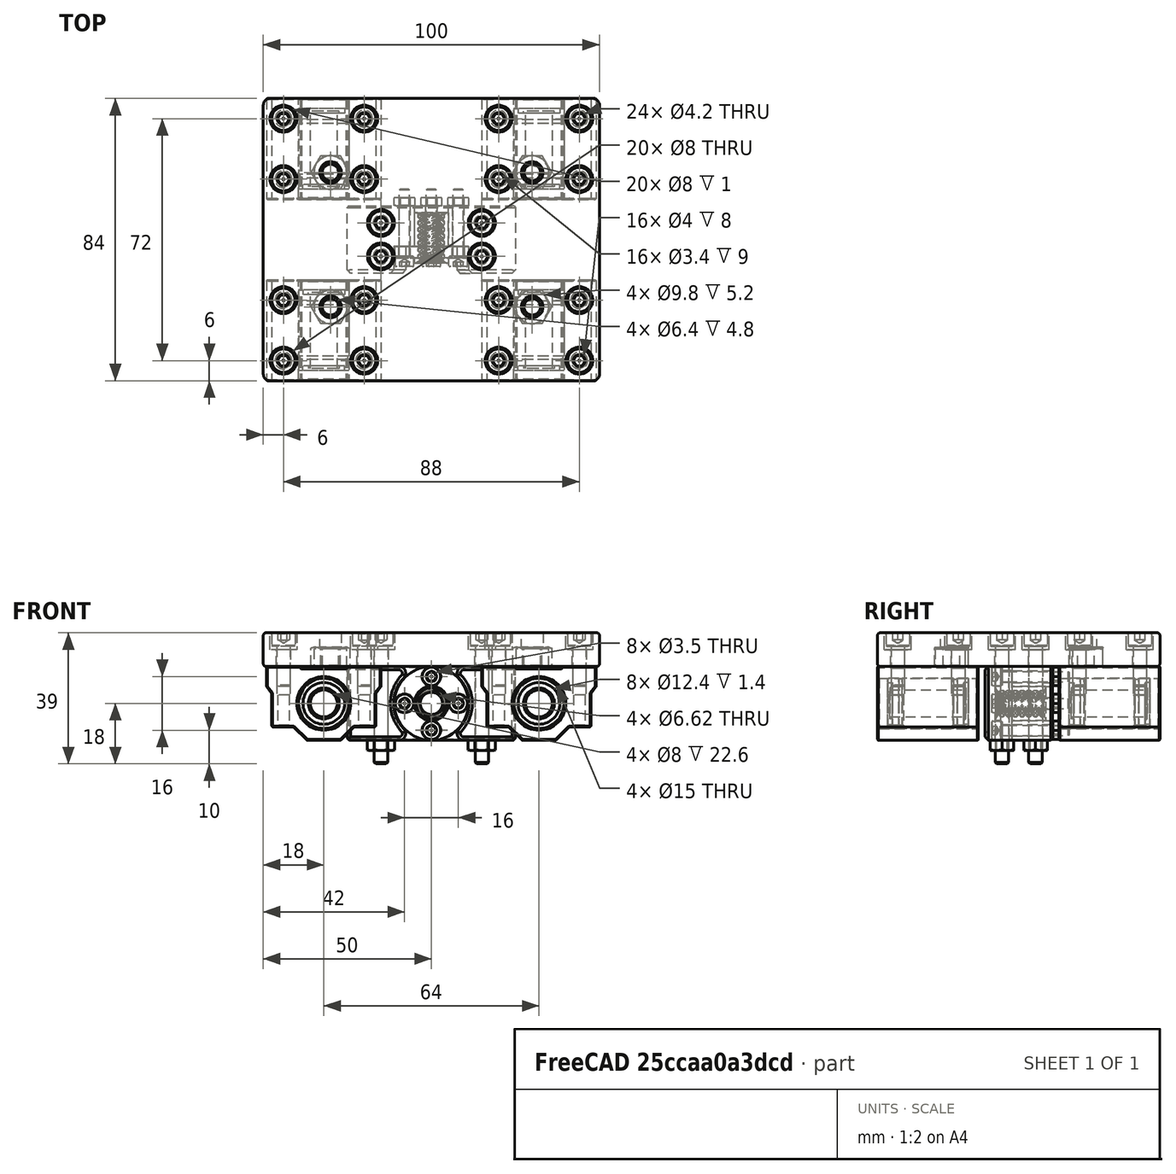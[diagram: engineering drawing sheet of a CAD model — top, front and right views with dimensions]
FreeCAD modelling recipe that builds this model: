
FCSTD DOCUMENT  (FreeCAD 0.19R)
Label: carriage_ass4
License: All rights reserved
LicenseURL: http://en.wikipedia.org/wiki/All_rights_reserved
objects: Part::FeaturePython×36, Part::Compound×18, Part::Feature×11
note: 65 computed .brp shape members not serialized (recipe doc carries the construction recipe); baked Part::Feature solids carry a one-line shape summary decoded from their .brp

FEATURE [Part::Feature] Chamfer002001  label="nutblock"
  Placement = pos=(25,32,-22) rot=(0,0,1;0rad)
  shape: bbox 50 x 20 x 22 mm, 53 faces (baked)
FEATURE [Part::Feature] Cut001  label="trapeznut"
  Placement = pos=(50,35,-11) rot=(0,0,1;1.5708rad)
  shape: bbox 22 x 24 x 22 mm, 53 faces (baked)
FEATURE [Part::FeaturePython] Screw  label="M4x12-Screw"  # Fasteners workbench fastener (typed FeaturePython)
  Placement = pos=(6,6,6) rot=(0,0,1;0rad)
  Visibility1 = false
  diameter = 5
  invert = false
  length = 3
  matchOuter = false
  offset = 0
  thread = false
  type = 15
FEATURE [Part::FeaturePython] Screw001  label="M4x12-Screw001"  # Fasteners workbench fastener (typed FeaturePython)
  Placement = pos=(30,6,6) rot=(0,0,1;0rad)
  Visibility1 = false
  diameter = 5
  invert = false
  length = 3
  matchOuter = false
  offset = 0
  thread = false
  type = 15
FEATURE [Part::FeaturePython] Screw002  label="M4x12-Screw002"  # Fasteners workbench fastener (typed FeaturePython)
  Placement = pos=(30,24,6) rot=(0,0,1;0rad)
  Visibility1 = false
  diameter = 5
  invert = false
  length = 3
  matchOuter = false
  offset = 0
  thread = false
  type = 15
FEATURE [Part::FeaturePython] Screw003  label="M4x12-Screw003"  # Fasteners workbench fastener (typed FeaturePython)
  Placement = pos=(6,24,6) rot=(0,0,1;0rad)
  Visibility1 = false
  diameter = 5
  invert = false
  length = 3
  matchOuter = false
  offset = 0
  thread = false
  type = 15
FEATURE [Part::Compound] Compound  label="m4x12_4er"
  Links = -> [Screw,Screw001,Screw002,Screw003]
FEATURE [Part::FeaturePython] Screw004  label="M4x12-Screw004"  # Fasteners workbench fastener (typed FeaturePython)
  Placement = pos=(30,6,6) rot=(0,0,1;0rad)
  Visibility1 = false
  diameter = 5
  invert = false
  length = 3
  matchOuter = false
  offset = 0
  thread = false
  type = 15
FEATURE [Part::FeaturePython] Screw005  label="M4x12-Screw005"  # Fasteners workbench fastener (typed FeaturePython)
  Placement = pos=(6,6,6) rot=(0,0,1;0rad)
  Visibility1 = false
  diameter = 5
  invert = false
  length = 3
  matchOuter = false
  offset = 0
  thread = false
  type = 15
FEATURE [Part::FeaturePython] Screw006  label="M4x12-Screw006"  # Fasteners workbench fastener (typed FeaturePython)
  Placement = pos=(30,24,6) rot=(0,0,1;0rad)
  Visibility1 = false
  diameter = 5
  invert = false
  length = 3
  matchOuter = false
  offset = 0
  thread = false
  type = 15
FEATURE [Part::FeaturePython] Screw007  label="M4x12-Screw007"  # Fasteners workbench fastener (typed FeaturePython)
  Placement = pos=(6,24,6) rot=(0,0,1;0rad)
  Visibility1 = false
  diameter = 5
  invert = false
  length = 3
  matchOuter = false
  offset = 0
  thread = false
  type = 15
FEATURE [Part::Compound] Compound001  label="m4x12_4er001"
  Links = -> [Screw005,Screw004,Screw006,Screw007]
  Placement = pos=(64,0,0) rot=(0,0,1;0rad)
FEATURE [Part::FeaturePython] Screw008  label="M4x12-Screw008"  # Fasteners workbench fastener (typed FeaturePython)
  Placement = pos=(30,6,6) rot=(0,0,1;0rad)
  Visibility1 = false
  diameter = 5
  invert = false
  length = 3
  matchOuter = false
  offset = 0
  thread = false
  type = 15
FEATURE [Part::FeaturePython] Screw009  label="M4x12-Screw009"  # Fasteners workbench fastener (typed FeaturePython)
  Placement = pos=(30,24,6) rot=(0,0,1;0rad)
  Visibility1 = false
  diameter = 5
  invert = false
  length = 3
  matchOuter = false
  offset = 0
  thread = false
  type = 15
FEATURE [Part::FeaturePython] Screw010  label="M4x12-Screw010"  # Fasteners workbench fastener (typed FeaturePython)
  Placement = pos=(6,24,6) rot=(0,0,1;0rad)
  Visibility1 = false
  diameter = 5
  invert = false
  length = 3
  matchOuter = false
  offset = 0
  thread = false
  type = 15
FEATURE [Part::FeaturePython] Screw011  label="M4x12-Screw011"  # Fasteners workbench fastener (typed FeaturePython)
  Placement = pos=(6,6,6) rot=(0,0,1;0rad)
  Visibility1 = false
  diameter = 5
  invert = false
  length = 3
  matchOuter = false
  offset = 0
  thread = false
  type = 15
FEATURE [Part::Compound] Compound002  label="m4x12_4er002"
  Links = -> [Screw011,Screw008,Screw009,Screw010]
  Placement = pos=(64,54,0) rot=(0,0,1;0rad)
FEATURE [Part::FeaturePython] Screw012  label="M4x12-Screw012"  # Fasteners workbench fastener (typed FeaturePython)
  Placement = pos=(6,6,6) rot=(0,0,1;0rad)
  Visibility1 = false
  diameter = 5
  invert = false
  length = 3
  matchOuter = false
  offset = 0
  thread = false
  type = 15
FEATURE [Part::FeaturePython] Screw013  label="M4x12-Screw013"  # Fasteners workbench fastener (typed FeaturePython)
  Placement = pos=(30,6,6) rot=(0,0,1;0rad)
  Visibility1 = false
  diameter = 5
  invert = false
  length = 3
  matchOuter = false
  offset = 0
  thread = false
  type = 15
FEATURE [Part::FeaturePython] Screw014  label="M4x12-Screw014"  # Fasteners workbench fastener (typed FeaturePython)
  Placement = pos=(30,24,6) rot=(0,0,1;0rad)
  Visibility1 = false
  diameter = 5
  invert = false
  length = 3
  matchOuter = false
  offset = 0
  thread = false
  type = 15
FEATURE [Part::FeaturePython] Screw015  label="M4x12-Screw015"  # Fasteners workbench fastener (typed FeaturePython)
  Placement = pos=(6,24,6) rot=(0,0,1;0rad)
  Visibility1 = false
  diameter = 5
  invert = false
  length = 3
  matchOuter = false
  offset = 0
  thread = false
  type = 15
FEATURE [Part::Compound] Compound003  label="m4x12_4er003"
  Links = -> [Screw012,Screw013,Screw014,Screw015]
  Placement = pos=(0,54,0) rot=(0,0,1;0rad)
FEATURE [Part::Compound] Compound004  label="m4x12ers"
  Links = -> [Compound,Compound001,Compound002,Compound003]
FEATURE [Part::FeaturePython] Screw016  label="M4x35-Screw"  # Fasteners workbench fastener (typed FeaturePython)
  Placement = pos=(35,37,6) rot=(0,0,1;0rad)
  Visibility1 = false
  diameter = 5
  invert = false
  length = 9
  matchOuter = false
  offset = 0
  thread = false
  type = 15
FEATURE [Part::FeaturePython] Screw017  label="M4x35-Screw001"  # Fasteners workbench fastener (typed FeaturePython)
  Placement = pos=(65,37,6) rot=(0,0,1;0rad)
  Visibility1 = false
  diameter = 5
  invert = false
  length = 9
  matchOuter = false
  offset = 0
  thread = false
  type = 15
FEATURE [Part::FeaturePython] Screw018  label="M4x35-Screw002"  # Fasteners workbench fastener (typed FeaturePython)
  Placement = pos=(65,47,6) rot=(0,0,1;0rad)
  Visibility1 = false
  diameter = 5
  invert = false
  length = 9
  matchOuter = false
  offset = 0
  thread = false
  type = 15
FEATURE [Part::FeaturePython] Screw019  label="M4x35-Screw003"  # Fasteners workbench fastener (typed FeaturePython)
  Placement = pos=(35,47,6) rot=(0,0,1;0rad)
  Visibility1 = false
  diameter = 5
  invert = false
  length = 9
  matchOuter = false
  offset = 0
  thread = false
  type = 15
FEATURE [Part::Compound] Compound005  label="m4x35ers"
  Links = -> [Screw016,Screw017,Screw018,Screw019]
FEATURE [Part::FeaturePython] Nut001  label="M4-Nut"  # Fasteners workbench fastener (typed FeaturePython)
  Placement = pos=(35,37,-25) rot=(0,0,1;0rad)
  Visibility1 = false
  diameter = 6
  invert = false
  matchOuter = false
  offset = 0
  thread = false
  type = 4
FEATURE [Part::FeaturePython] Nut002  label="M4-Nut001"  # Fasteners workbench fastener (typed FeaturePython)
  Placement = pos=(35,47,-25) rot=(0,0,1;0rad)
  Visibility1 = false
  diameter = 6
  invert = false
  matchOuter = false
  offset = 0
  thread = false
  type = 4
FEATURE [Part::FeaturePython] Nut003  label="M4-Nut002"  # Fasteners workbench fastener (typed FeaturePython)
  Placement = pos=(65,47,-25) rot=(0,0,1;0rad)
  Visibility1 = false
  diameter = 6
  invert = false
  matchOuter = false
  offset = 0
  thread = false
  type = 4
FEATURE [Part::FeaturePython] Nut004  label="M4-Nut003"  # Fasteners workbench fastener (typed FeaturePython)
  Placement = pos=(65,37,-25) rot=(0,0,1;0rad)
  Visibility1 = false
  diameter = 6
  invert = false
  matchOuter = false
  offset = 0
  thread = false
  type = 4
FEATURE [Part::Compound] Compound006  label="m4nuts"
  Links = -> [Nut001,Nut002,Nut003,Nut004]
FEATURE [Part::FeaturePython] Nut  label="M6-Nut"  # Fasteners workbench fastener (typed FeaturePython)
  Placement = pos=(20,22,0) rot=(0,0,1;0rad)
  Visibility1 = false
  diameter = 2
  invert = false
  matchOuter = false
  offset = 0
  thread = false
  type = 2
FEATURE [Part::FeaturePython] Nut005  label="M6-Nut001"  # Fasteners workbench fastener (typed FeaturePython)
  Placement = pos=(80,22,0) rot=(0,0,1;0rad)
  Visibility1 = false
  diameter = 2
  invert = false
  matchOuter = false
  offset = 0
  thread = false
  type = 2
FEATURE [Part::FeaturePython] Nut006  label="M6-Nut004"  # Fasteners workbench fastener (typed FeaturePython)
  Placement = pos=(20,62,0) rot=(0,0,1;0rad)
  Visibility1 = false
  diameter = 2
  invert = false
  matchOuter = false
  offset = 0
  thread = false
  type = 2
FEATURE [Part::FeaturePython] Nut007  label="M6-Nut003"  # Fasteners workbench fastener (typed FeaturePython)
  Placement = pos=(80,62,0) rot=(0,0,1;0rad)
  Visibility1 = false
  diameter = 2
  invert = false
  matchOuter = false
  offset = 0
  thread = false
  type = 2
FEATURE [Part::Compound] Compound007  label="m6nuts"
  Links = -> [Nut,Nut005,Nut006,Nut007]
FEATURE [Part::FeaturePython] Screw020  label="M3x20-Screw"  # Fasteners workbench fastener (typed FeaturePython)
  Placement = pos=(50,37,-19) rot=(1,0,0;1.5708rad)
  Visibility1 = false
  diameter = 4
  invert = false
  length = 7
  matchOuter = false
  offset = 0
  thread = false
  type = 15
FEATURE [Part::FeaturePython] Nut008  label="M3-Nut"  # Fasteners workbench fastener (typed FeaturePython)
  Placement = pos=(50,54.5,-19) rot=(1,0,0;1.5708rad)
  Visibility1 = false
  diameter = 4
  invert = false
  matchOuter = false
  offset = 0
  thread = false
  type = 4
FEATURE [Part::Compound] Compound008  label="m3x20screwnut"
  Links = -> [Screw020,Nut008]
  Placement = pos=(8,0,8) rot=(0,0,1;0rad)
FEATURE [Part::FeaturePython] Screw021  label="M3x20-Screw001"  # Fasteners workbench fastener (typed FeaturePython)
  Placement = pos=(50,37,-19) rot=(1,0,0;1.5708rad)
  Visibility1 = false
  diameter = 4
  invert = false
  length = 7
  matchOuter = false
  offset = 0
  thread = false
  type = 15
FEATURE [Part::FeaturePython] Nut009  label="M3-Nut001"  # Fasteners workbench fastener (typed FeaturePython)
  Placement = pos=(50,54.5,-19) rot=(1,0,0;1.5708rad)
  Visibility1 = false
  diameter = 4
  invert = false
  matchOuter = false
  offset = 0
  thread = false
  type = 4
FEATURE [Part::Compound] Compound009  label="m3x20screwnut001"
  Links = -> [Screw021,Nut009]
  Placement = pos=(0,0,16) rot=(0,0,1;0rad)
FEATURE [Part::FeaturePython] Screw022  label="M3x20-Screw002"  # Fasteners workbench fastener (typed FeaturePython)
  Placement = pos=(50,37,-19) rot=(1,0,0;1.5708rad)
  Visibility1 = false
  diameter = 4
  invert = false
  length = 7
  matchOuter = false
  offset = 0
  thread = false
  type = 15
FEATURE [Part::FeaturePython] Nut010  label="M3-Nut002"  # Fasteners workbench fastener (typed FeaturePython)
  Placement = pos=(50,54.5,-19) rot=(1,0,0;1.5708rad)
  Visibility1 = false
  diameter = 4
  invert = false
  matchOuter = false
  offset = 0
  thread = false
  type = 4
FEATURE [Part::Compound] Compound010  label="m3x20screwnut002"
  Links = -> [Screw022,Nut010]
FEATURE [Part::FeaturePython] Screw023  label="M3x20-Screw003"  # Fasteners workbench fastener (typed FeaturePython)
  Placement = pos=(50,37,-19) rot=(1,0,0;1.5708rad)
  Visibility1 = false
  diameter = 4
  invert = false
  length = 7
  matchOuter = false
  offset = 0
  thread = false
  type = 15
FEATURE [Part::FeaturePython] Nut011  label="M3-Nut003"  # Fasteners workbench fastener (typed FeaturePython)
  Placement = pos=(50,54.5,-19) rot=(1,0,0;1.5708rad)
  Visibility1 = false
  diameter = 4
  invert = false
  matchOuter = false
  offset = 0
  thread = false
  type = 4
FEATURE [Part::Compound] Compound011  label="m3x20screwnut003"
  Links = -> [Screw023,Nut011]
  Placement = pos=(-8,0,8) rot=(0,0,1;0rad)
FEATURE [Part::Compound] Compound012  label="m3x20screwnuts"
  Links = -> [Compound008,Compound009,Compound010,Compound011]
FEATURE [Part::Feature] Fillet002001  label="carriageplate2"
  shape: bbox 100.3 x 84.33 x 10 mm, 118 faces (baked)
FEATURE [Part::Feature] Body001  label="SC8UU"
  shape: bbox 34 x 30 x 22 mm, 85 faces (baked)
FEATURE [Part::Feature] Revolution001  label="LM8UU"
  Placement = pos=(0,-15,-10.5) rot=(1,0,0;3.14159rad)
  shape: bbox 15 x 24 x 15 mm, 20 faces (baked)
FEATURE [Part::Compound] Compound013  label="SC8UU+LM8UU"
  Links = -> [Revolution001,Body001]
  Placement = pos=(18,30,-0.5) rot=(0,0,1;0rad)
FEATURE [Part::Feature] Body002  label="SC8UU001"
  shape: bbox 34 x 30 x 22 mm, 85 faces (baked)
FEATURE [Part::Feature] Revolution002  label="LM8UU001"
  Placement = pos=(0,-15,-10.5) rot=(1,0,0;3.14159rad)
  shape: bbox 15 x 24 x 15 mm, 20 faces (baked)
FEATURE [Part::Compound] Compound014  label="SC8UU+LM8UU001"
  Links = -> [Revolution002,Body002]
  Placement = pos=(82,30,-0.5) rot=(0,0,1;0rad)
FEATURE [Part::Feature] Revolution003  label="LM8UU002"
  Placement = pos=(0,-15,-10.5) rot=(1,0,0;3.14159rad)
  shape: bbox 15 x 24 x 15 mm, 20 faces (baked)
FEATURE [Part::Feature] Body003  label="SC8UU002"
  shape: bbox 34 x 30 x 22 mm, 85 faces (baked)
FEATURE [Part::Compound] Compound015  label="SC8UU+LM8UU002"
  Links = -> [Revolution003,Body003]
  Placement = pos=(82,84,-0.5) rot=(0,0,1;0rad)
FEATURE [Part::Feature] Body004  label="SC8UU003"
  shape: bbox 34 x 30 x 22 mm, 85 faces (baked)
FEATURE [Part::Feature] Revolution004  label="LM8UU003"
  Placement = pos=(0,-15,-10.5) rot=(1,0,0;3.14159rad)
  shape: bbox 15 x 24 x 15 mm, 20 faces (baked)
FEATURE [Part::Compound] Compound016  label="SC8UU+LM8UU003"
  Links = -> [Revolution004,Body004]
  Placement = pos=(18,84,-0.5) rot=(0,0,1;0rad)
FEATURE [Part::Compound] Compound017  label="carriage_ass4-Modul"
  Links = -> [Chamfer002001,Cut001,Compound004,Compound005,Compound006,Compound007,Compound012,Fillet002001,Compound013,Compound014,Compound015,Compound016]
